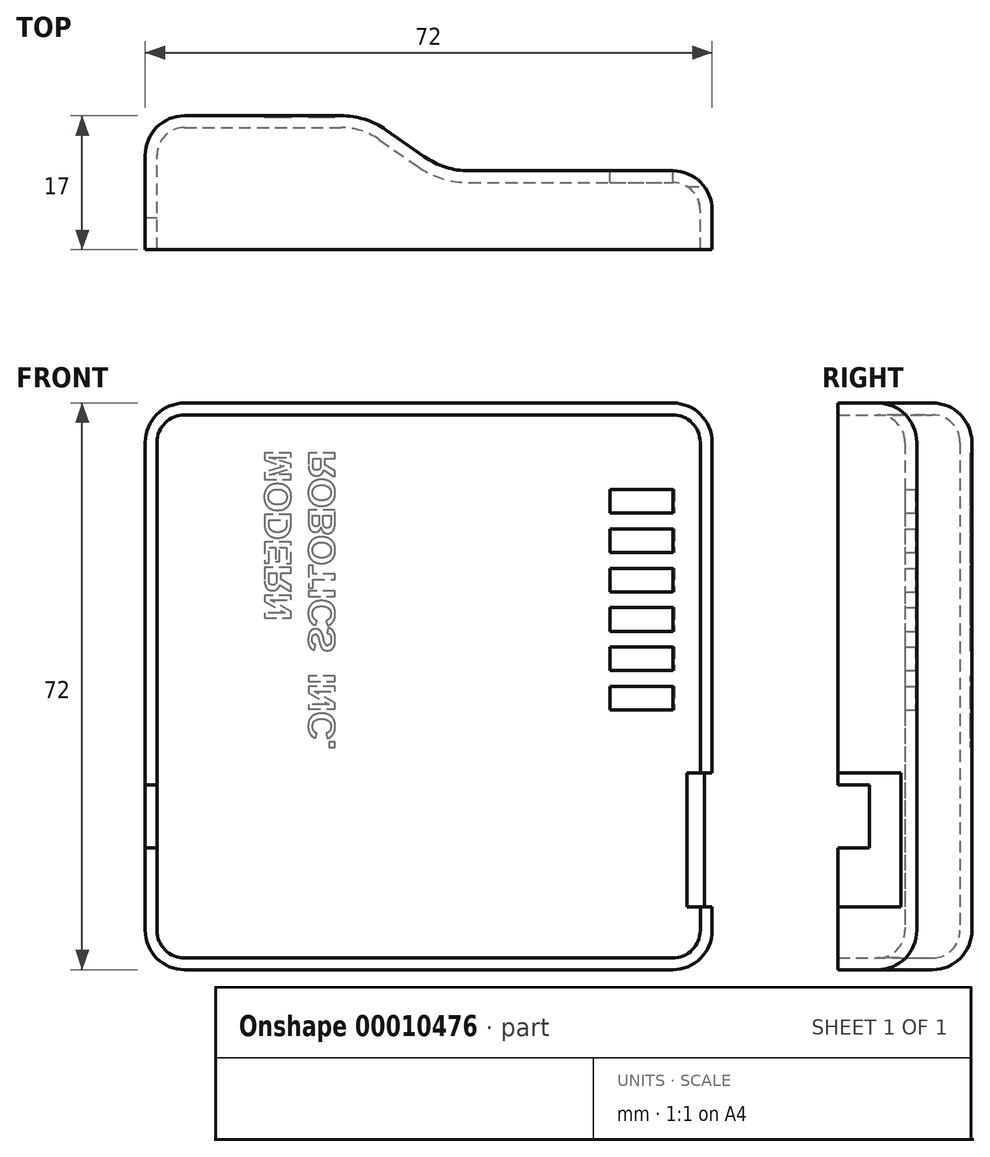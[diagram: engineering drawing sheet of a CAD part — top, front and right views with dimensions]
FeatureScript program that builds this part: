
annotation { "Feature Type Name" : "Feature", "Feature Type Description" : "" }
export const myFeature = defineFeature(function(context is Context, id is Id, definition is map)
    precondition{}
    {
        {
            var Q0;
            Q0=qCreatedBy(makeId("Top.planeOp"),FACE);
            var sketch = newSketch(context, id + "F0", { "sketchPlane" : qUnion([Q0])});
            skPoint(sketch, "E0.visualSharp", {"position": v(28, 17) * mm});
            skPoint(sketch, "E1.visualSharp", {"position": v(38, 10) * mm});
            skLineSegment(sketch, "E2", {"start": v(0, 0) * mm, "end": v(72, 0) * mm});
            skLineSegment(sketch, "E3", {"start": v(72, 10) * mm, "end": v(41.15, 10) * mm});
            skLineSegment(sketch, "E4", {"start": v(72, 0) * mm, "end": v(72, 10) * mm});
            skLineSegment(sketch, "E5", {"start": v(24.85, 17) * mm, "end": v(0, 17) * mm});
            skLineSegment(sketch, "E6", {"start": v(35.42, 11.8) * mm, "end": v(30.58, 15.2) * mm});
            skArc(sketch, "E0.filletArc", {"start": v(30.58, 15.2) * mm, "mid": v(27.85, 16.54) * mm, "end": v(24.85, 17) * mm});
            skLineSegment(sketch, "E7", {"start": v(0, 17) * mm, "end": v(0, 0) * mm});
            skArc(sketch, "E1.filletArc", {"start": v(35.42, 11.8) * mm, "mid": v(38.15, 10.46) * mm, "end": v(41.15, 10) * mm});
            skSolve(sketch);
        }
        {
            var Q0;
            Q0=qSketchRegion(id+"F0",true);
            extrude(context, id + "F1", {"entities" : qUnion([Q0]), "depth" : 72 * mm});
        }
        {
            var Q0;
            Q0=makeQuery(id+"F1.opExtrude","CAP_EDGE",EDGE,{"disambiguationData":[OSD([sQuery(id+"F0.wireOp",EDGE,"E5")])],"isStart":false});
            var Q1;
            Q1=makeQuery(id+"F1.opExtrude","SWEPT_EDGE",EDGE,{"disambiguationData":[OSD([sQuery(id+"F0.wireOp",EDGE,"E3"),sQuery(id+"F0.wireOp",EDGE,"E4")])]});
            var Q2;
            Q2=makeQuery(id+"F1.opExtrude","CAP_EDGE",EDGE,{"disambiguationData":[OSD([sQuery(id+"F0.wireOp",EDGE,"E3")])],"isStart":true});
            var Q3;
            Q3=makeQuery(id+"F1.opExtrude","SWEPT_EDGE",EDGE,{"disambiguationData":[OSD([sQuery(id+"F0.wireOp",EDGE,"E5"),sQuery(id+"F0.wireOp",EDGE,"E7")])]});
            var Q4;
            Q4=makeQuery(id+"F1.opExtrude","CAP_EDGE",EDGE,{"disambiguationData":[OSD([sQuery(id+"F0.wireOp",EDGE,"E7")])],"isStart":false});
            var Q5;
            Q5=makeQuery(id+"F1.opExtrude","CAP_EDGE",EDGE,{"disambiguationData":[OSD([sQuery(id+"F0.wireOp",EDGE,"E4")])],"isStart":false});
            var Q6;
            Q6=makeQuery(id+"F1.opExtrude","CAP_EDGE",EDGE,{"disambiguationData":[OSD([sQuery(id+"F0.wireOp",EDGE,"E4")])],"isStart":true});
            var Q7;
            Q7=makeQuery(id+"F1.opExtrude","CAP_EDGE",EDGE,{"disambiguationData":[OSD([sQuery(id+"F0.wireOp",EDGE,"E7")])],"isStart":true});
            fillet(context, id + "F2", {"entities" : qUnion([Q0, Q1, Q2, Q3, Q4, Q5, Q6, Q7]), "radius" : 5 * mm, "tangentPropagation" : true, "allowEdgeOverflow" : false});
        }
        {
            var Q0;
            Q0=makeQuery(id+"F1.opExtrude","SWEPT_FACE",FACE,{"disambiguationData":[OSD([sQuery(id+"F0.wireOp",EDGE,"E2")])]});
            var Q1;
            Q1=makeQuery(id+"F1.opExtrude","SWEPT_BODY",BODY,{"disambiguationData":[OSD([sQuery(id+"F0.wireOp",EDGE,"E2"),sQuery(id+"F0.wireOp",EDGE,"E3"),sQuery(id+"F0.wireOp",EDGE,"E4"),sQuery(id+"F0.wireOp",EDGE,"E5"),sQuery(id+"F0.wireOp",EDGE,"E6"),sQuery(id+"F0.wireOp",EDGE,"E0.filletArc"),sQuery(id+"F0.wireOp",EDGE,"E7"),sQuery(id+"F0.wireOp",EDGE,"E1.filletArc")])]});
            shell(context, id + "F3", {"entities" : qUnion([Q0]), "parts" : qUnion([Q1]), "thickness" : 1.5 * mm});
        }
        {
            var Q0;
            Q0=makeQuery(id+"F1.opExtrude","SWEPT_FACE",FACE,{"disambiguationData":[OSD([sQuery(id+"F0.wireOp",EDGE,"E7")])]});
            var sketch = newSketch(context, id + "F4", { "sketchPlane" : qUnion([Q0])});
            skLineSegment(sketch, "E8.bottom", {"start": v(0, 23.5) * mm, "end": v(-4, 23.5) * mm});
            skLineSegment(sketch, "E8.top", {"start": v(0, 15.5) * mm, "end": v(-4, 15.5) * mm});
            skLineSegment(sketch, "E8.left", {"start": v(0, 23.5) * mm, "end": v(0, 15.5) * mm});
            skLineSegment(sketch, "E8.right", {"start": v(-4, 23.5) * mm, "end": v(-4, 15.5) * mm});
            skSolve(sketch);
        }
        {
            var Q0;
            Q0=qSketchRegion(id+"F4",true);
            extrude(context, id + "F5", {"entities" : qUnion([Q0]), "operationType" : NewBodyOperationType.REMOVE, "endBound" : BoundingType.UP_TO_NEXT, "oppositeDirection" : true, "depth" : 25 * mm});
        }
        {
            var Q0;
            Q0=makeQuery(id+"F1.opExtrude","SWEPT_FACE",FACE,{"disambiguationData":[OSD([sQuery(id+"F0.wireOp",EDGE,"E5")])]});
            var sketch = newSketch(context, id + "F6", { "sketchPlane" : qUnion([Q0])});
            skText(sketch, "E9", { "text": "MODERN\nROBOTICS  INC.", "fontName": "Arimo-Bold.ttf"});
            const initialGuessF6  = {"E9": [-0.0185, 0.066, 0, -1, 0.0035]};
            skSetInitialGuess(sketch, initialGuessF6);
            skSolve(sketch);
        }
        {
            var Q0;
            Q0=qSketchRegion(id+"F6",true);
            extrude(context, id + "F7", {"entities" : qUnion([Q0]), "operationType" : NewBodyOperationType.REMOVE, "oppositeDirection" : true, "depth" : .2 * mm});
        }
        {
            var Q0;
            Q0=makeQuery(id+"F1.opExtrude","SWEPT_FACE",FACE,{"disambiguationData":[OSD([sQuery(id+"F0.wireOp",EDGE,"E3")])]});
            var sketch = newSketch(context, id + "F8", { "sketchPlane" : qUnion([Q0])});
            skLineSegment(sketch, "E10.bottom", {"start": v(-59, 61) * mm, "end": v(-67, 61) * mm});
            skLineSegment(sketch, "E10.top", {"start": v(-59, 58) * mm, "end": v(-67, 58) * mm});
            skLineSegment(sketch, "E10.left", {"start": v(-59, 61) * mm, "end": v(-59, 58) * mm});
            skLineSegment(sketch, "E10.right", {"start": v(-67, 61) * mm, "end": v(-67, 58) * mm});
            skLineSegment(sketch, "E11.0.1.0", {"start": v(-59, 56) * mm, "end": v(-67, 56) * mm});
            skLineSegment(sketch, "E11.0.1.1", {"start": v(-59, 53) * mm, "end": v(-67, 53) * mm});
            skLineSegment(sketch, "E11.0.1.2", {"start": v(-59, 56) * mm, "end": v(-59, 53) * mm});
            skLineSegment(sketch, "E11.0.1.3", {"start": v(-67, 56) * mm, "end": v(-67, 53) * mm});
            skLineSegment(sketch, "E11.0.2.0", {"start": v(-59, 51) * mm, "end": v(-67, 51) * mm});
            skLineSegment(sketch, "E11.0.2.1", {"start": v(-59, 48) * mm, "end": v(-67, 48) * mm});
            skLineSegment(sketch, "E11.0.2.2", {"start": v(-59, 51) * mm, "end": v(-59, 48) * mm});
            skLineSegment(sketch, "E11.0.2.3", {"start": v(-67, 51) * mm, "end": v(-67, 48) * mm});
            skLineSegment(sketch, "E11.0.3.0", {"start": v(-59, 46) * mm, "end": v(-67, 46) * mm});
            skLineSegment(sketch, "E11.0.3.1", {"start": v(-59, 43) * mm, "end": v(-67, 43) * mm});
            skLineSegment(sketch, "E11.0.3.2", {"start": v(-59, 46) * mm, "end": v(-59, 43) * mm});
            skLineSegment(sketch, "E11.0.3.3", {"start": v(-67, 46) * mm, "end": v(-67, 43) * mm});
            skLineSegment(sketch, "E11.0.4.0", {"start": v(-59, 41) * mm, "end": v(-67, 41) * mm});
            skLineSegment(sketch, "E11.0.4.1", {"start": v(-59, 38) * mm, "end": v(-67, 38) * mm});
            skLineSegment(sketch, "E11.0.4.2", {"start": v(-59, 41) * mm, "end": v(-59, 38) * mm});
            skLineSegment(sketch, "E11.0.4.3", {"start": v(-67, 41) * mm, "end": v(-67, 38) * mm});
            skLineSegment(sketch, "E11.0.5.0", {"start": v(-59, 36) * mm, "end": v(-67, 36) * mm});
            skLineSegment(sketch, "E11.0.5.1", {"start": v(-59, 33) * mm, "end": v(-67, 33) * mm});
            skLineSegment(sketch, "E11.0.5.2", {"start": v(-59, 36) * mm, "end": v(-59, 33) * mm});
            skLineSegment(sketch, "E11.0.5.3", {"start": v(-67, 36) * mm, "end": v(-67, 33) * mm});
            skLineSegment(sketch, "E11.direction1", {"start": v(-67, 61) * mm, "end": v(-42, 61) * mm, "construction": true});
            skLineSegment(sketch, "E11.direction2", {"start": v(-67, 61) * mm, "end": v(-67, 56) * mm, "construction": true});
            skSolve(sketch);
        }
        {
            var Q0;
            Q0 = qSketchRegion(id + "F8", true);
            extrude(context, id + "F9", {"entities" : qUnion([Q0]), "operationType" : NewBodyOperationType.REMOVE, "endBound" : BoundingType.UP_TO_NEXT, "oppositeDirection" : true, "depth" : 25 * mm});
        }
        {
            var Q0;
            {var subQ0=sQuery(id+"F0.wireOp",EDGE,"E3");Q0=makeQuery(id+"F9.boolean.opBoolean","MERGE",EDGE,{"derivedFrom":[makeQuery(id+"F2.opFillet","BLEND_EDGE",EDGE,{"blendedFrom":[makeQuery(id+"F1.opExtrude","SWEPT_EDGE",EDGE,{"disambiguationData":[OSD([subQ0,sQuery(id+"F0.wireOp",EDGE,"E4")])]}),makeQuery(id+"F1.opExtrude","SWEPT_FACE",FACE,{"disambiguationData":[OSD([subQ0])]})],"blendedInto":[makeQuery(id+"F1.opExtrude","SWEPT_FACE",FACE,{"disambiguationData":[OSD([subQ0])]})]}),makeQuery(id+"F9.opExtrude","CAP_EDGE",EDGE,{"disambiguationData":[OSD([sQuery(id+"F8.wireOp",EDGE,"E10.right")])],"isStart":true})]});}
            var Q1;
            Q1=makeQuery(id+"F9.boolean.opBoolean","COPY",EDGE,{"derivedFrom":makeQuery(id+"F9.opExtrude","CAP_EDGE",EDGE,{"disambiguationData":[OSD([sQuery(id+"F8.wireOp",EDGE,"E10.bottom")])],"isStart":true})});
            var Q2;
            Q2=makeQuery(id+"F9.boolean.opBoolean","COPY",EDGE,{"derivedFrom":makeQuery(id+"F9.opExtrude","CAP_EDGE",EDGE,{"disambiguationData":[OSD([sQuery(id+"F8.wireOp",EDGE,"E10.left")])],"isStart":true})});
            var Q3;
            Q3=makeQuery(id+"F9.boolean.opBoolean","COPY",EDGE,{"derivedFrom":makeQuery(id+"F9.opExtrude","CAP_EDGE",EDGE,{"disambiguationData":[OSD([sQuery(id+"F8.wireOp",EDGE,"E10.top")])],"isStart":true})});
            var Q4;
            Q4=makeQuery(id+"F9.boolean.opBoolean","COPY",EDGE,{"derivedFrom":makeQuery(id+"F9.opExtrude","CAP_EDGE",EDGE,{"disambiguationData":[OSD([sQuery(id+"F8.wireOp",EDGE,"E11.0.1.0")])],"isStart":true})});
            var Q5;
            {var subQ0=sQuery(id+"F0.wireOp",EDGE,"E3");Q5=makeQuery(id+"F9.boolean.opBoolean","MERGE",EDGE,{"derivedFrom":[makeQuery(id+"F2.opFillet","BLEND_EDGE",EDGE,{"blendedFrom":[makeQuery(id+"F1.opExtrude","SWEPT_EDGE",EDGE,{"disambiguationData":[OSD([subQ0,sQuery(id+"F0.wireOp",EDGE,"E4")])]}),makeQuery(id+"F1.opExtrude","SWEPT_FACE",FACE,{"disambiguationData":[OSD([subQ0])]})],"blendedInto":[makeQuery(id+"F1.opExtrude","SWEPT_FACE",FACE,{"disambiguationData":[OSD([subQ0])]})]}),makeQuery(id+"F9.opExtrude","CAP_EDGE",EDGE,{"disambiguationData":[OSD([sQuery(id+"F8.wireOp",EDGE,"E11.0.1.3")])],"isStart":true})]});}
            var Q6;
            Q6=makeQuery(id+"F9.boolean.opBoolean","COPY",EDGE,{"derivedFrom":makeQuery(id+"F9.opExtrude","CAP_EDGE",EDGE,{"disambiguationData":[OSD([sQuery(id+"F8.wireOp",EDGE,"E11.0.1.2")])],"isStart":true})});
            var Q7;
            Q7=makeQuery(id+"F9.boolean.opBoolean","COPY",EDGE,{"derivedFrom":makeQuery(id+"F9.opExtrude","CAP_EDGE",EDGE,{"disambiguationData":[OSD([sQuery(id+"F8.wireOp",EDGE,"E11.0.1.1")])],"isStart":true})});
            var Q8;
            Q8=makeQuery(id+"F9.boolean.opBoolean","COPY",EDGE,{"derivedFrom":makeQuery(id+"F9.opExtrude","CAP_EDGE",EDGE,{"disambiguationData":[OSD([sQuery(id+"F8.wireOp",EDGE,"E11.0.2.2")])],"isStart":true})});
            var Q9;
            Q9=makeQuery(id+"F9.boolean.opBoolean","COPY",EDGE,{"derivedFrom":makeQuery(id+"F9.opExtrude","CAP_EDGE",EDGE,{"disambiguationData":[OSD([sQuery(id+"F8.wireOp",EDGE,"E11.0.2.0")])],"isStart":true})});
            var Q10;
            {var subQ0=sQuery(id+"F0.wireOp",EDGE,"E3");Q10=makeQuery(id+"F9.boolean.opBoolean","MERGE",EDGE,{"derivedFrom":[makeQuery(id+"F2.opFillet","BLEND_EDGE",EDGE,{"blendedFrom":[makeQuery(id+"F1.opExtrude","SWEPT_EDGE",EDGE,{"disambiguationData":[OSD([subQ0,sQuery(id+"F0.wireOp",EDGE,"E4")])]}),makeQuery(id+"F1.opExtrude","SWEPT_FACE",FACE,{"disambiguationData":[OSD([subQ0])]})],"blendedInto":[makeQuery(id+"F1.opExtrude","SWEPT_FACE",FACE,{"disambiguationData":[OSD([subQ0])]})]}),makeQuery(id+"F9.opExtrude","CAP_EDGE",EDGE,{"disambiguationData":[OSD([sQuery(id+"F8.wireOp",EDGE,"E11.0.2.3")])],"isStart":true})]});}
            var Q11;
            Q11=makeQuery(id+"F9.boolean.opBoolean","COPY",EDGE,{"derivedFrom":makeQuery(id+"F9.opExtrude","CAP_EDGE",EDGE,{"disambiguationData":[OSD([sQuery(id+"F8.wireOp",EDGE,"E11.0.2.1")])],"isStart":true})});
            var Q12;
            Q12=makeQuery(id+"F9.boolean.opBoolean","COPY",EDGE,{"derivedFrom":makeQuery(id+"F9.opExtrude","CAP_EDGE",EDGE,{"disambiguationData":[OSD([sQuery(id+"F8.wireOp",EDGE,"E11.0.3.1")])],"isStart":true})});
            var Q13;
            {var subQ0=sQuery(id+"F0.wireOp",EDGE,"E3");Q13=makeQuery(id+"F9.boolean.opBoolean","MERGE",EDGE,{"derivedFrom":[makeQuery(id+"F2.opFillet","BLEND_EDGE",EDGE,{"blendedFrom":[makeQuery(id+"F1.opExtrude","SWEPT_EDGE",EDGE,{"disambiguationData":[OSD([subQ0,sQuery(id+"F0.wireOp",EDGE,"E4")])]}),makeQuery(id+"F1.opExtrude","SWEPT_FACE",FACE,{"disambiguationData":[OSD([subQ0])]})],"blendedInto":[makeQuery(id+"F1.opExtrude","SWEPT_FACE",FACE,{"disambiguationData":[OSD([subQ0])]})]}),makeQuery(id+"F9.opExtrude","CAP_EDGE",EDGE,{"disambiguationData":[OSD([sQuery(id+"F8.wireOp",EDGE,"E11.0.3.3")])],"isStart":true})]});}
            var Q14;
            Q14=makeQuery(id+"F9.boolean.opBoolean","COPY",EDGE,{"derivedFrom":makeQuery(id+"F9.opExtrude","CAP_EDGE",EDGE,{"disambiguationData":[OSD([sQuery(id+"F8.wireOp",EDGE,"E11.0.3.0")])],"isStart":true})});
            var Q15;
            Q15=makeQuery(id+"F9.boolean.opBoolean","COPY",EDGE,{"derivedFrom":makeQuery(id+"F9.opExtrude","CAP_EDGE",EDGE,{"disambiguationData":[OSD([sQuery(id+"F8.wireOp",EDGE,"E11.0.3.2")])],"isStart":true})});
            var Q16;
            Q16=makeQuery(id+"F9.boolean.opBoolean","COPY",EDGE,{"derivedFrom":makeQuery(id+"F9.opExtrude","CAP_EDGE",EDGE,{"disambiguationData":[OSD([sQuery(id+"F8.wireOp",EDGE,"E11.0.4.2")])],"isStart":true})});
            var Q17;
            Q17=makeQuery(id+"F9.boolean.opBoolean","COPY",EDGE,{"derivedFrom":makeQuery(id+"F9.opExtrude","CAP_EDGE",EDGE,{"disambiguationData":[OSD([sQuery(id+"F8.wireOp",EDGE,"E11.0.4.0")])],"isStart":true})});
            var Q18;
            {var subQ0=sQuery(id+"F0.wireOp",EDGE,"E3");Q18=makeQuery(id+"F9.boolean.opBoolean","MERGE",EDGE,{"derivedFrom":[makeQuery(id+"F2.opFillet","BLEND_EDGE",EDGE,{"blendedFrom":[makeQuery(id+"F1.opExtrude","SWEPT_EDGE",EDGE,{"disambiguationData":[OSD([subQ0,sQuery(id+"F0.wireOp",EDGE,"E4")])]}),makeQuery(id+"F1.opExtrude","SWEPT_FACE",FACE,{"disambiguationData":[OSD([subQ0])]})],"blendedInto":[makeQuery(id+"F1.opExtrude","SWEPT_FACE",FACE,{"disambiguationData":[OSD([subQ0])]})]}),makeQuery(id+"F9.opExtrude","CAP_EDGE",EDGE,{"disambiguationData":[OSD([sQuery(id+"F8.wireOp",EDGE,"E11.0.4.3")])],"isStart":true})]});}
            var Q19;
            Q19=makeQuery(id+"F9.boolean.opBoolean","COPY",EDGE,{"derivedFrom":makeQuery(id+"F9.opExtrude","CAP_EDGE",EDGE,{"disambiguationData":[OSD([sQuery(id+"F8.wireOp",EDGE,"E11.0.4.1")])],"isStart":true})});
            var Q20;
            Q20=makeQuery(id+"F9.boolean.opBoolean","COPY",EDGE,{"derivedFrom":makeQuery(id+"F9.opExtrude","CAP_EDGE",EDGE,{"disambiguationData":[OSD([sQuery(id+"F8.wireOp",EDGE,"E11.0.5.2")])],"isStart":true})});
            var Q21;
            {var subQ0=sQuery(id+"F0.wireOp",EDGE,"E3");Q21=makeQuery(id+"F9.boolean.opBoolean","MERGE",EDGE,{"derivedFrom":[makeQuery(id+"F2.opFillet","BLEND_EDGE",EDGE,{"blendedFrom":[makeQuery(id+"F1.opExtrude","SWEPT_EDGE",EDGE,{"disambiguationData":[OSD([subQ0,sQuery(id+"F0.wireOp",EDGE,"E4")])]}),makeQuery(id+"F1.opExtrude","SWEPT_FACE",FACE,{"disambiguationData":[OSD([subQ0])]})],"blendedInto":[makeQuery(id+"F1.opExtrude","SWEPT_FACE",FACE,{"disambiguationData":[OSD([subQ0])]})]}),makeQuery(id+"F9.opExtrude","CAP_EDGE",EDGE,{"disambiguationData":[OSD([sQuery(id+"F8.wireOp",EDGE,"E11.0.5.3")])],"isStart":true})]});}
            var Q22;
            Q22=makeQuery(id+"F9.boolean.opBoolean","COPY",EDGE,{"derivedFrom":makeQuery(id+"F9.opExtrude","CAP_EDGE",EDGE,{"disambiguationData":[OSD([sQuery(id+"F8.wireOp",EDGE,"E11.0.5.0")])],"isStart":true})});
            var Q23;
            Q23=makeQuery(id+"F9.boolean.opBoolean","COPY",EDGE,{"derivedFrom":makeQuery(id+"F9.opExtrude","CAP_EDGE",EDGE,{"disambiguationData":[OSD([sQuery(id+"F8.wireOp",EDGE,"E11.0.5.1")])],"isStart":true})});
            chamfer(context, id + "F10", {"entities" : qUnion([Q0, Q1, Q2, Q3, Q4, Q5, Q6, Q7, Q8, Q9, Q10, Q11, Q12, Q13, Q14, Q15, Q16, Q17, Q18, Q19, Q20, Q21, Q22, Q23]), "width" : .2 * mm, "tangentPropagation" : true});
        }
        {
            var Q0;
            Q0=makeQuery(id+"F1.opExtrude","SWEPT_FACE",FACE,{"disambiguationData":[OSD([sQuery(id+"F0.wireOp",EDGE,"E4")])]});
            var sketch = newSketch(context, id + "F11", { "sketchPlane" : qUnion([Q0])});
            skLineSegment(sketch, "E12.bottom", {"start": v(0, 25) * mm, "end": v(8, 25) * mm});
            skLineSegment(sketch, "E12.left", {"start": v(0, 25) * mm, "end": v(0, 8) * mm});
            skLineSegment(sketch, "E12.right", {"start": v(8, 25) * mm, "end": v(8, 8) * mm});
            skLineSegment(sketch, "E12.top", {"start": v(0, 8) * mm, "end": v(8, 8) * mm});
            skSolve(sketch);
        }
        {
            var Q0;
            Q0 = qSketchRegion(id + "F11", true);
            extrude(context, id + "F12", {"entities" : qUnion([Q0]), "operationType" : NewBodyOperationType.REMOVE, "endBound" : BoundingType.UP_TO_NEXT, "oppositeDirection" : true, "depth" : 25 * mm});
        }
    });
